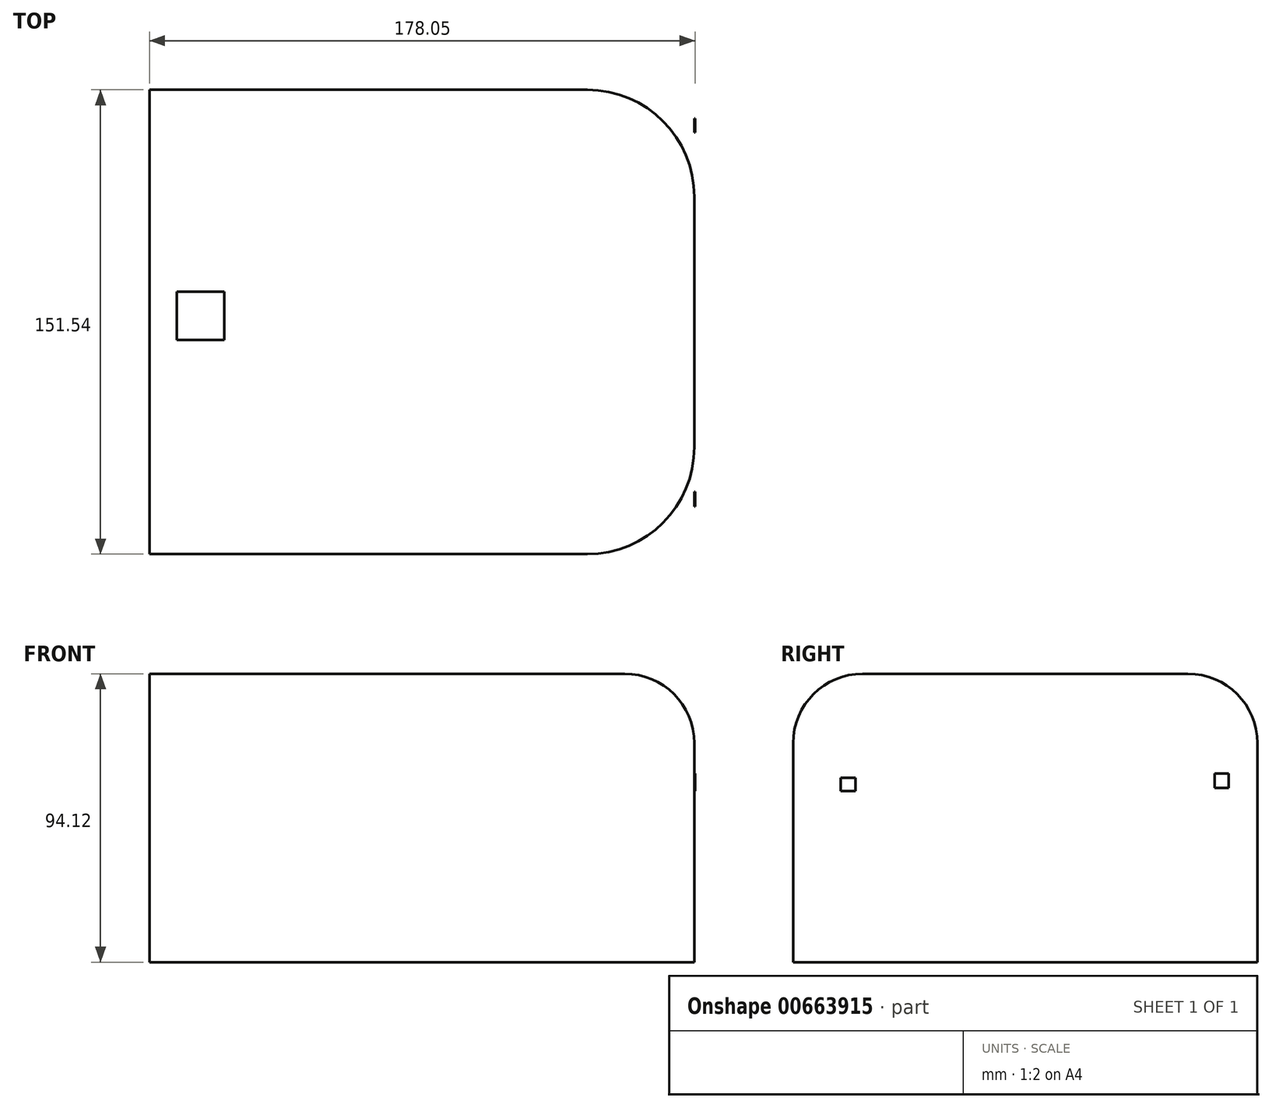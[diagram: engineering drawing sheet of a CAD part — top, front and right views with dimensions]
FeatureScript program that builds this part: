
annotation { "Feature Type Name" : "Feature", "Feature Type Description" : "" }
export const myFeature = defineFeature(function(context is Context, id is Id, definition is map)
    precondition{}
    {
        {
            var Q0;
            Q0=qCreatedBy(makeId("Right.planeOp"),FACE);
            var sketch = newSketch(context, id + "F0", { "sketchPlane" : qUnion([Q0])});
            skLineSegment(sketch, "E0.bottom", {"start": v(-137.55, 67.86) * mm, "end": v(13.99, 67.86) * mm});
            skLineSegment(sketch, "E0.top", {"start": v(-137.55, -26.23) * mm, "end": v(13.99, -26.23) * mm});
            skLineSegment(sketch, "E0.left", {"start": v(-137.55, 67.86) * mm, "end": v(-137.55, -26.23) * mm});
            skLineSegment(sketch, "E0.right", {"start": v(13.99, 67.86) * mm, "end": v(13.99, -26.23) * mm});
            skSolve(sketch);
        }
        {
            var Q0;
            Q0 = qSketchRegion(id + "F0", true);
            extrude(context, id + "F1", {"entities" : qUnion([Q0]), "depth" : 76.2 * mm, "offsetDistance" : 25.4 * mm});
        }
        {
            var Q0;
            Q0=makeQuery(id+"F1.opExtrude","CAP_FACE",FACE,{"disambiguationData":[OSD([sQuery(id+"F0.wireOp",EDGE,"E0.bottom"),sQuery(id+"F0.wireOp",EDGE,"E0.top"),sQuery(id+"F0.wireOp",EDGE,"E0.left"),sQuery(id+"F0.wireOp",EDGE,"E0.right")])],"isStart":true});
            extrude(context, id + "F2", {"entities" : qUnion([Q0]), "operationType" : NewBodyOperationType.ADD, "depth" : 101.6 * mm, "offsetDistance" : 25.4 * mm});
        }
        {
            var Q0;
            Q0=makeQuery(id+"F1.opExtrude","CAP_EDGE",EDGE,{"disambiguationData":[OSD([sQuery(id+"F0.wireOp",EDGE,"E0.left")])],"isStart":false});
            var Q1;
            Q1=makeQuery(id+"F1.opExtrude","CAP_EDGE",EDGE,{"disambiguationData":[OSD([sQuery(id+"F0.wireOp",EDGE,"E0.right")])],"isStart":false});
            fillet(context, id + "F3", {"entities" : qUnion([Q0, Q1]), "radius" : 34.95 * mm, "tangentPropagation" : true, "allowEdgeOverflow" : false});
        }
        {
            var Q0;
            Q0=makeQuery(id+"F1.opExtrude","CAP_EDGE",EDGE,{"disambiguationData":[OSD([sQuery(id+"F0.wireOp",EDGE,"E0.bottom")])],"isStart":false});
            fillet(context, id + "F4", {"entities" : qUnion([Q0]), "radius" : 22.7 * mm, "tangentPropagation" : true, "allowEdgeOverflow" : false});
        }
        {
            var Q0;
            {var subQ0=sQuery(id+"F0.wireOp",EDGE,"E0.bottom");Q0=makeQuery(id+"F2.boolean.opBoolean","MERGE",FACE,{"derivedFrom":[makeQuery(id+"F1.opExtrude","SWEPT_FACE",FACE,{"disambiguationData":[OSD([subQ0])]}),makeQuery(id+"F2.opExtrude","SWEPT_FACE",FACE,{"disambiguationData":[OSD([subQ0])]})]});}
            var sketch = newSketch(context, id + "F5", { "sketchPlane" : qUnion([Q0])});
            skLineSegment(sketch, "E1.bottom", {"start": v(-92.64, -51.9) * mm, "end": v(-77.16, -51.9) * mm});
            skLineSegment(sketch, "E1.top", {"start": v(-92.64, -67.59) * mm, "end": v(-77.16, -67.59) * mm});
            skLineSegment(sketch, "E1.left", {"start": v(-92.64, -51.9) * mm, "end": v(-92.64, -67.59) * mm});
            skLineSegment(sketch, "E1.right", {"start": v(-77.16, -51.9) * mm, "end": v(-77.16, -67.59) * mm});
            skSolve(sketch);
        }
        {
            var Q0;
            Q0 = qSketchRegion(id + "F5", true);
            extrude(context, id + "F6", {"entities" : qUnion([Q0]), "operationType" : NewBodyOperationType.ADD, "depth" : 0.03 * mm, "offsetDistance" : 25.4 * mm});
        }
        {
            var Q0;
            Q0=makeQuery(id+"F1.opExtrude","CAP_FACE",FACE,{"disambiguationData":[OSD([sQuery(id+"F0.wireOp",EDGE,"E0.bottom"),sQuery(id+"F0.wireOp",EDGE,"E0.top"),sQuery(id+"F0.wireOp",EDGE,"E0.left"),sQuery(id+"F0.wireOp",EDGE,"E0.right")])],"isStart":false});
            var sketch = newSketch(context, id + "F7", { "sketchPlane" : qUnion([Q0])});
            skLineSegment(sketch, "E2.bottom", {"start": v(-123.5, 36.12) * mm, "end": v(-119.46, 36.12) * mm});
            skLineSegment(sketch, "E2.top", {"start": v(-123.5, 30.65) * mm, "end": v(-119.46, 30.65) * mm});
            skLineSegment(sketch, "E2.left", {"start": v(-123.5, 36.12) * mm, "end": v(-123.5, 30.65) * mm});
            skLineSegment(sketch, "E2.right", {"start": v(-119.46, 36.12) * mm, "end": v(-119.46, 30.65) * mm});
            skLineSegment(sketch, "E3.bottom", {"start": v(0, 30.65) * mm, "end": v(4.58, 30.65) * mm});
            skLineSegment(sketch, "E3.top", {"start": v(0, 35.26) * mm, "end": v(4.58, 35.26) * mm});
            skLineSegment(sketch, "E3.left", {"start": v(0, 30.65) * mm, "end": v(0, 35.26) * mm});
            skLineSegment(sketch, "E3.right", {"start": v(4.58, 30.65) * mm, "end": v(4.58, 35.26) * mm});
            skSolve(sketch);
        }
        {
            var Q0;
            Q0=makeQuery(id+"F7.imprint","IMPRINT",FACE,{"disambiguationData":[TD([[makeQuery(id+"F7.imprint","IMPRINT",EDGE,{"derivedFrom":sQuery(id+"F7.wireOp",EDGE,"E3.bottom")}),1.0]])]});
            extrude(context, id + "F8", {"entities" : qUnion([Q0]), "depth" : 0.25 * mm, "offsetDistance" : 25.4 * mm});
        }
        {
            var Q0;
            Q0=makeQuery(id+"F1.opExtrude","CAP_FACE",FACE,{"disambiguationData":[OSD([sQuery(id+"F0.wireOp",EDGE,"E0.bottom"),sQuery(id+"F0.wireOp",EDGE,"E0.top"),sQuery(id+"F0.wireOp",EDGE,"E0.left"),sQuery(id+"F0.wireOp",EDGE,"E0.right")])],"isStart":false});
            var sketch = newSketch(context, id + "F9", { "sketchPlane" : qUnion([Q0])});
            skLineSegment(sketch, "E4.bottom", {"start": v(-117.16, 33.86) * mm, "end": v(-122.05, 33.86) * mm});
            skLineSegment(sketch, "E4.top", {"start": v(-117.16, 29.55) * mm, "end": v(-122.05, 29.55) * mm});
            skLineSegment(sketch, "E4.left", {"start": v(-117.16, 33.86) * mm, "end": v(-117.16, 29.55) * mm});
            skLineSegment(sketch, "E4.right", {"start": v(-122.05, 33.86) * mm, "end": v(-122.05, 29.55) * mm});
            skSolve(sketch);
        }
        {
            var Q0;
            Q0 = qSketchRegion(id + "F9", true);
            extrude(context, id + "F10", {"entities" : qUnion([Q0]), "depth" : 0.25 * mm, "offsetDistance" : 25.4 * mm});
        }
    });
